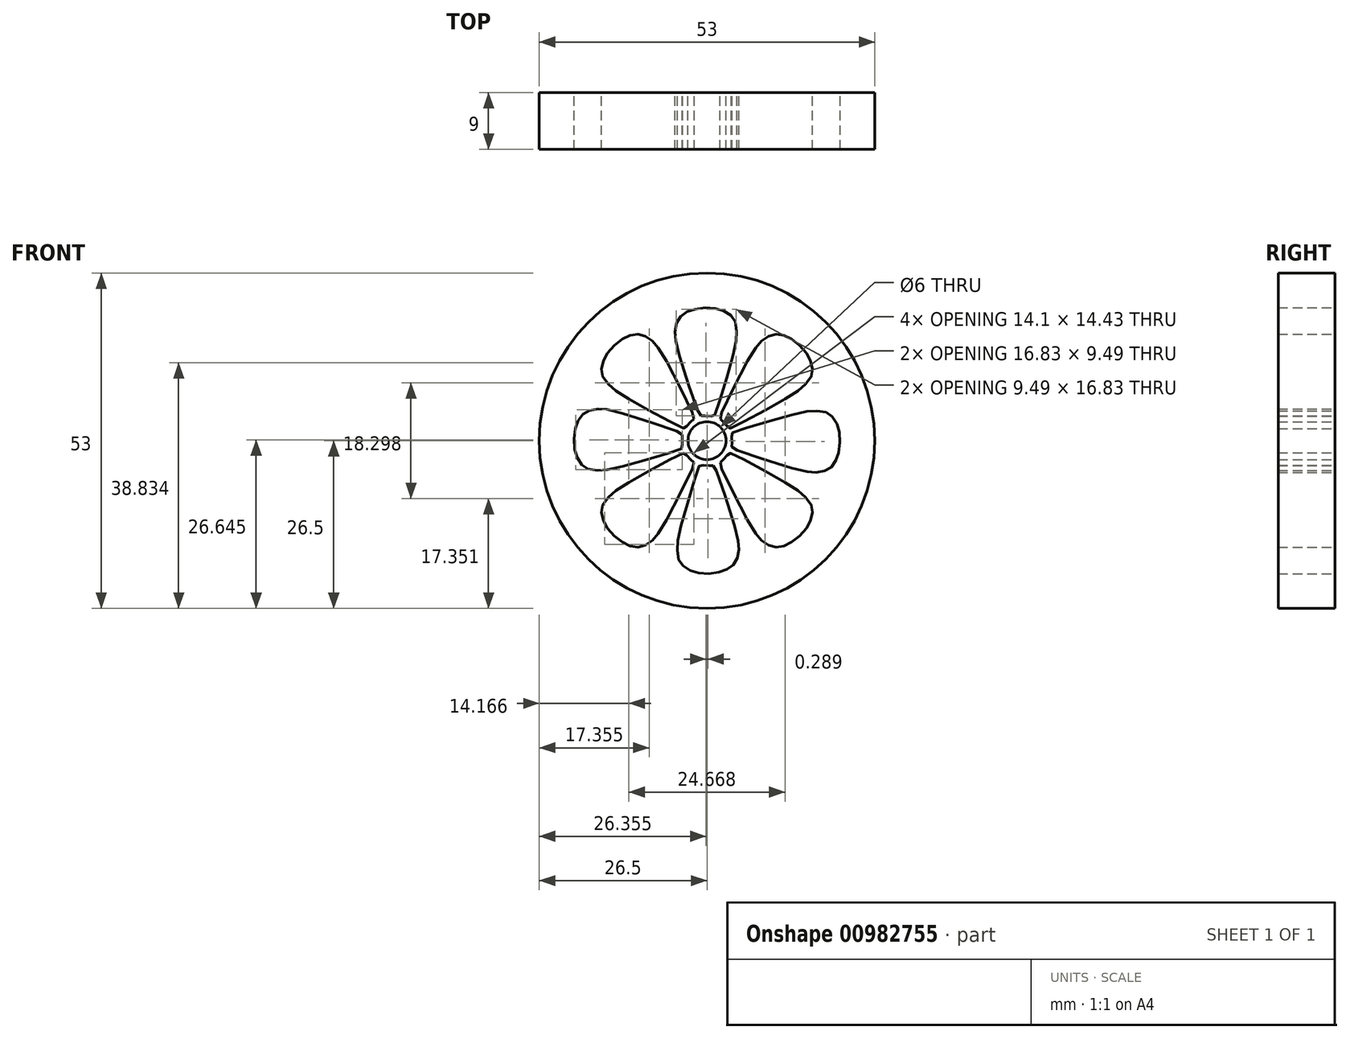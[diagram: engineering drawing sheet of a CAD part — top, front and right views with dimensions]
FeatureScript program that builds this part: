
annotation { "Feature Type Name" : "Feature", "Feature Type Description" : "" }
export const myFeature = defineFeature(function(context is Context, id is Id, definition is map)
    precondition{}
    {
        {
            var Q0;
            Q0=qCreatedBy(makeId("Front.planeOp"),FACE);
            var sketch = newSketch(context, id + "F0", { "sketchPlane" : qUnion([Q0])});
            skCircle(sketch, "E0", {"center": v(0, 0) * mm, "radius": 3 * mm});
            skFitSpline(sketch, "E1", {"points": [v(-0.96, 3.92) * mm, v(-1.11, 4) * mm, v(-1.38, 4.47) * mm, v(-4.52, 14) * mm, v(-4.97, 16.21) * mm, v(-5.03, 17.24) * mm, v(-4.88, 18.3) * mm, v(-4.52, 19.15) * mm, v(-4.1, 19.72) * mm, v(-3.37, 20.24) * mm, v(-2.55, 20.6) * mm, v(-1.5, 20.87) * mm, v(0, 21.02) * mm, v(1.35, 20.9) * mm, v(2.35, 20.63) * mm, v(3.32, 20.14) * mm, v(3.99, 19.6) * mm, v(4.4, 19) * mm, v(4.65, 17.94) * mm, v(4.68, 16.6) * mm, v(4.44, 14.88) * mm, v(2.84, 9.01) * mm, v(1.3, 4.1) * mm, v(1.14, 3.88) * mm, v(1.01, 3.86) * mm, v(0.6, 3.9) * mm, v(0, 3.94) * mm, v(-0.36, 3.93) * mm, v(-0.67, 3.9) * mm, v(-0.9, 3.9) * mm, v(-0.96, 3.92) * mm]});
            skLineSegment(sketch, "E2", {"start": v(0, 21.02) * mm, "end": v(0, 0) * mm, "construction": true});
            skCircle(sketch, "E3", {"center": v(0, 0) * mm, "radius": 21.02 * mm, "construction": true});
            skLineSegment(sketch, "E4.1.0", {"start": v(-14.87, 14.87) * mm, "end": v(0, 0) * mm, "construction": true});
            skLineSegment(sketch, "E4.2.0", {"start": v(-21.02, 0) * mm, "end": v(0, 0) * mm, "construction": true});
            skLineSegment(sketch, "E4.3.0", {"start": v(-14.87, -14.87) * mm, "end": v(0, 0) * mm, "construction": true});
            skLineSegment(sketch, "E4.4.0", {"start": v(0, -21.02) * mm, "end": v(0, 0) * mm, "construction": true});
            skLineSegment(sketch, "E4.5.0", {"start": v(14.87, -14.87) * mm, "end": v(0, 0) * mm, "construction": true});
            skLineSegment(sketch, "E4.6.0", {"start": v(21.02, 0) * mm, "end": v(0, 0) * mm, "construction": true});
            skLineSegment(sketch, "E4.7.0", {"start": v(14.87, 14.87) * mm, "end": v(0, 0) * mm, "construction": true});
            skFitSpline(sketch, "E5", {"points": [v(2.1, 3.45) * mm, v(2.04, 3.61) * mm, v(2.18, 4.13) * mm, v(6.7, 13.1) * mm, v(7.95, 14.98) * mm, v(8.63, 15.75) * mm, v(9.49, 16.39) * mm, v(10.35, 16.73) * mm, v(11.05, 16.84) * mm, v(11.93, 16.69) * mm, v(12.76, 16.37) * mm, v(13.7, 15.81) * mm, v(14.87, 14.87) * mm, v(15.74, 13.82) * mm, v(16.25, 12.92) * mm, v(16.6, 11.9) * mm, v(16.68, 11.04) * mm, v(16.55, 10.31) * mm, v(15.97, 9.4) * mm, v(15.05, 8.43) * mm, v(13.66, 7.38) * mm, v(8.38, 4.37) * mm, v(3.82, 2) * mm, v(3.55, 1.93) * mm, v(3.45, 2.02) * mm, v(3.17, 2.33) * mm, v(2.79, 2.79) * mm, v(2.52, 3.03) * mm, v(2.29, 3.23) * mm, v(2.13, 3.4) * mm, v(2.1, 3.45) * mm]});
            skFitSpline(sketch, "E6.MirrorC", {"points": [v(-3.92, 0.96) * mm, v(-4, 1.11) * mm, v(-4.47, 1.38) * mm, v(-14, 4.52) * mm, v(-16.21, 4.97) * mm, v(-17.24, 5.03) * mm, v(-18.3, 4.88) * mm, v(-19.15, 4.52) * mm, v(-19.72, 4.1) * mm, v(-20.24, 3.37) * mm, v(-20.6, 2.55) * mm, v(-20.87, 1.5) * mm, v(-21.02, 0) * mm, v(-20.9, -1.35) * mm, v(-20.63, -2.35) * mm, v(-20.14, -3.32) * mm, v(-19.6, -3.99) * mm, v(-19, -4.4) * mm, v(-17.94, -4.65) * mm, v(-16.6, -4.68) * mm, v(-14.88, -4.44) * mm, v(-9.01, -2.84) * mm, v(-4.1, -1.3) * mm, v(-3.88, -1.14) * mm, v(-3.86, -1.01) * mm, v(-3.9, -0.6) * mm, v(-3.94, 0) * mm, v(-3.93, 0.36) * mm, v(-3.9, 0.67) * mm, v(-3.9, 0.9) * mm, v(-3.92, 0.96) * mm]});
            skFitSpline(sketch, "E7.MirrorC", {"points": [v(0.96, -3.92) * mm, v(1.11, -4) * mm, v(1.38, -4.47) * mm, v(4.52, -14) * mm, v(4.97, -16.21) * mm, v(5.03, -17.24) * mm, v(4.88, -18.3) * mm, v(4.52, -19.15) * mm, v(4.1, -19.72) * mm, v(3.37, -20.24) * mm, v(2.55, -20.6) * mm, v(1.5, -20.87) * mm, v(0, -21.02) * mm, v(-1.35, -20.9) * mm, v(-2.35, -20.63) * mm, v(-3.32, -20.14) * mm, v(-3.99, -19.6) * mm, v(-4.4, -19) * mm, v(-4.65, -17.94) * mm, v(-4.68, -16.6) * mm, v(-4.44, -14.88) * mm, v(-2.84, -9.01) * mm, v(-1.3, -4.1) * mm, v(-1.14, -3.88) * mm, v(-1.01, -3.86) * mm, v(-0.6, -3.9) * mm, v(0, -3.94) * mm, v(0.36, -3.93) * mm, v(0.67, -3.9) * mm, v(0.9, -3.9) * mm, v(0.96, -3.92) * mm]});
            skFitSpline(sketch, "E8.MirrorC", {"points": [v(3.92, -0.96) * mm, v(4, -1.11) * mm, v(4.47, -1.38) * mm, v(14, -4.52) * mm, v(16.21, -4.97) * mm, v(17.24, -5.03) * mm, v(18.3, -4.88) * mm, v(19.15, -4.52) * mm, v(19.72, -4.1) * mm, v(20.24, -3.37) * mm, v(20.6, -2.55) * mm, v(20.87, -1.5) * mm, v(21.02, 0) * mm, v(20.9, 1.35) * mm, v(20.63, 2.35) * mm, v(20.14, 3.32) * mm, v(19.6, 3.99) * mm, v(19, 4.4) * mm, v(17.94, 4.65) * mm, v(16.6, 4.68) * mm, v(14.88, 4.44) * mm, v(9.01, 2.84) * mm, v(4.1, 1.3) * mm, v(3.88, 1.14) * mm, v(3.86, 1.01) * mm, v(3.9, 0.6) * mm, v(3.94, 0) * mm, v(3.93, -0.36) * mm, v(3.9, -0.67) * mm, v(3.9, -0.9) * mm, v(3.92, -0.96) * mm]});
            skFitSpline(sketch, "E9.MirrorC", {"points": [v(2.1, -3.45) * mm, v(2.04, -3.61) * mm, v(2.18, -4.13) * mm, v(6.7, -13.1) * mm, v(7.95, -14.98) * mm, v(8.63, -15.75) * mm, v(9.49, -16.39) * mm, v(10.35, -16.73) * mm, v(11.05, -16.84) * mm, v(11.93, -16.69) * mm, v(12.76, -16.37) * mm, v(13.7, -15.81) * mm, v(14.87, -14.87) * mm, v(15.74, -13.82) * mm, v(16.25, -12.92) * mm, v(16.6, -11.9) * mm, v(16.68, -11.04) * mm, v(16.55, -10.31) * mm, v(15.97, -9.4) * mm, v(15.05, -8.43) * mm, v(13.66, -7.38) * mm, v(8.38, -4.37) * mm, v(3.82, -2) * mm, v(3.55, -1.93) * mm, v(3.45, -2.02) * mm, v(3.17, -2.33) * mm, v(2.79, -2.79) * mm, v(2.52, -3.03) * mm, v(2.29, -3.23) * mm, v(2.13, -3.4) * mm, v(2.1, -3.45) * mm]});
            skFitSpline(sketch, "E10.MirrorC", {"points": [v(-2.1, 3.45) * mm, v(-2.04, 3.61) * mm, v(-2.18, 4.13) * mm, v(-6.7, 13.1) * mm, v(-7.95, 14.98) * mm, v(-8.63, 15.75) * mm, v(-9.49, 16.39) * mm, v(-10.35, 16.73) * mm, v(-11.05, 16.84) * mm, v(-11.93, 16.69) * mm, v(-12.76, 16.37) * mm, v(-13.7, 15.81) * mm, v(-14.87, 14.87) * mm, v(-15.74, 13.82) * mm, v(-16.25, 12.92) * mm, v(-16.6, 11.9) * mm, v(-16.68, 11.04) * mm, v(-16.55, 10.31) * mm, v(-15.97, 9.4) * mm, v(-15.05, 8.43) * mm, v(-13.66, 7.38) * mm, v(-8.38, 4.37) * mm, v(-3.82, 2) * mm, v(-3.55, 1.93) * mm, v(-3.45, 2.02) * mm, v(-3.17, 2.33) * mm, v(-2.79, 2.79) * mm, v(-2.52, 3.03) * mm, v(-2.29, 3.23) * mm, v(-2.13, 3.4) * mm, v(-2.1, 3.45) * mm]});
            skFitSpline(sketch, "E11.MirrorC", {"points": [v(-2.1, -3.45) * mm, v(-2.04, -3.61) * mm, v(-2.18, -4.13) * mm, v(-6.7, -13.1) * mm, v(-7.95, -14.98) * mm, v(-8.63, -15.75) * mm, v(-9.49, -16.39) * mm, v(-10.35, -16.73) * mm, v(-11.05, -16.84) * mm, v(-11.93, -16.69) * mm, v(-12.76, -16.37) * mm, v(-13.7, -15.81) * mm, v(-14.87, -14.87) * mm, v(-15.74, -13.82) * mm, v(-16.25, -12.92) * mm, v(-16.6, -11.9) * mm, v(-16.68, -11.04) * mm, v(-16.55, -10.31) * mm, v(-15.97, -9.4) * mm, v(-15.05, -8.43) * mm, v(-13.66, -7.38) * mm, v(-8.38, -4.37) * mm, v(-3.82, -2) * mm, v(-3.55, -1.93) * mm, v(-3.45, -2.02) * mm, v(-3.17, -2.33) * mm, v(-2.79, -2.79) * mm, v(-2.52, -3.03) * mm, v(-2.29, -3.23) * mm, v(-2.13, -3.4) * mm, v(-2.1, -3.45) * mm]});
            skCircle(sketch, "E12", {"center": v(0, 0) * mm, "radius": 26.5 * mm});
            skSolve(sketch);
        }
        {
            var Q0;
            Q0=makeQuery(id+"F0.imprint","IMPRINT",FACE,{"disambiguationData":[TD([[makeQuery(id+"F0.imprint","IMPRINT",EDGE,{"derivedFrom":sQuery(id+"F0.wireOp",EDGE,"E0")}),-1.0]])]});
            extrude(context, id + "F1", {"entities" : qUnion([Q0]), "endBound" : BoundingType.SYMMETRIC, "depth" : 9 * mm, "offsetDistance" : 25 * mm});
        }
    });
